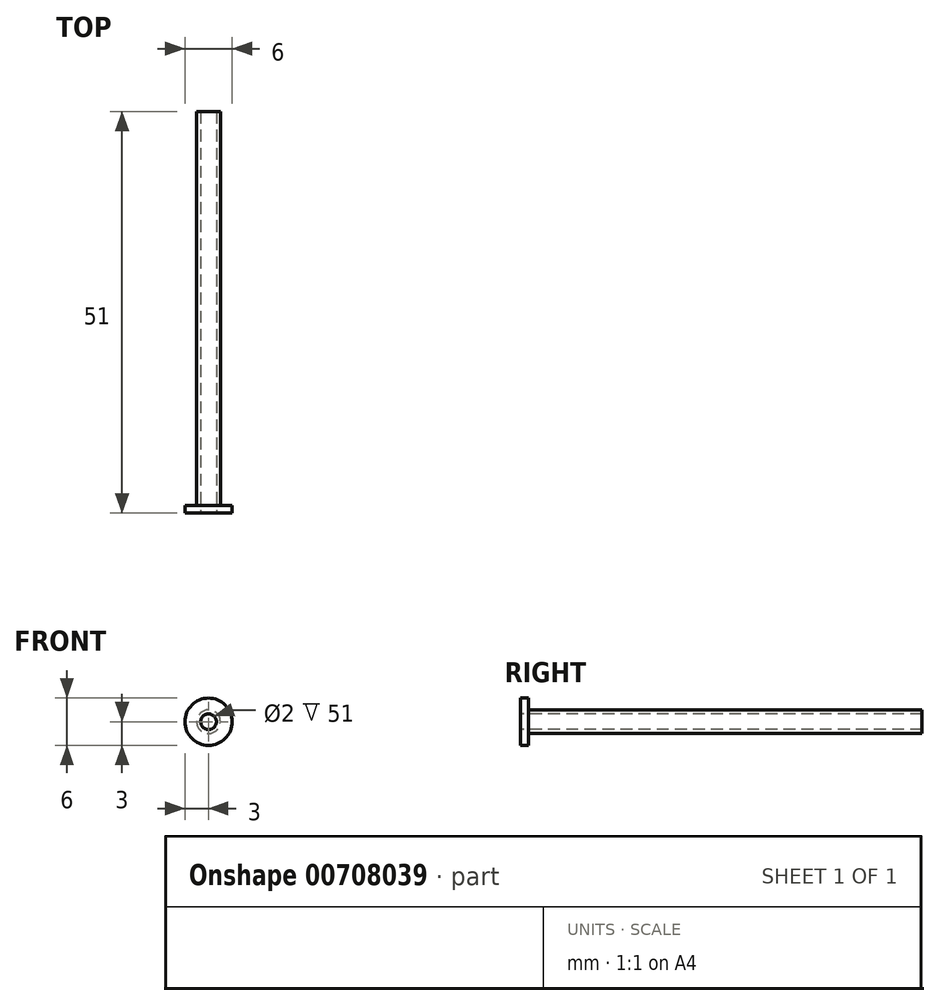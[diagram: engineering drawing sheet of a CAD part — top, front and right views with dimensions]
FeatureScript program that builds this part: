
annotation { "Feature Type Name" : "Feature", "Feature Type Description" : "" }
export const myFeature = defineFeature(function(context is Context, id is Id, definition is map)
    precondition{}
    {
        {
            var Q0;
            Q0=qCreatedBy(makeId("Front.planeOp"),FACE);
            var sketch = newSketch(context, id + "F0", { "sketchPlane" : qUnion([Q0])});
            skCircle(sketch, "E0", {"center": v(0, 0) * mm, "radius": 1.5 * mm});
            skSolve(sketch);
        }
        {
            var Q0;
            Q0 = qSketchRegion(id + "F0", true);
            extrude(context, id + "F1", {"entities" : qUnion([Q0]), "depth" : 50 * mm, "offsetDistance" : 25 * mm});
        }
        {
            var Q0;
            Q0=makeQuery(id+"F1.opExtrude","CAP_FACE",FACE,{"disambiguationData":[OSD([sQuery(id+"F0.wireOp",EDGE,"E0")])],"isStart":false});
            var sketch = newSketch(context, id + "F2", { "sketchPlane" : qUnion([Q0])});
            skCircle(sketch, "E1", {"center": v(0, 0) * mm, "radius": 1 * mm});
            skSolve(sketch);
        }
        {
            var Q0;
            Q0 = qSketchRegion(id + "F2", true);
            extrude(context, id + "F3", {"entities" : qUnion([Q0]), "operationType" : NewBodyOperationType.REMOVE, "endBound" : BoundingType.THROUGH_ALL, "oppositeDirection" : true, "depth" : 25 * mm, "offsetDistance" : 25 * mm});
        }
        {
            var Q0;
            Q0=makeQuery(id+"F1.opExtrude","CAP_FACE",FACE,{"disambiguationData":[OSD([sQuery(id+"F0.wireOp",EDGE,"E0")])],"isStart":false});
            var sketch = newSketch(context, id + "F4", { "sketchPlane" : qUnion([Q0])});
            skCircle(sketch, "E2", {"center": v(0, 0) * mm, "radius": 3 * mm});
            skSolve(sketch);
        }
        {
            var Q0;
            Q0=makeQuery(id+"F4.imprint","IMPRINT",FACE,{"disambiguationData":[TD([[makeQuery(id+"F4.imprint","IMPRINT",EDGE,{"derivedFrom":sQuery(id+"F4.wireOp",EDGE,"E2")}),1.0]])]});
            var sketch = newSketch(context, id + "F5", { "sketchPlane" : qUnion([Q0])});
            skCircle(sketch, "E3", {"center": v(0, 0) * mm, "radius": 1 * mm});
            skSolve(sketch);
        }
        {
            var Q0;
            Q0=makeQuery(id+"F4.imprint","IMPRINT",FACE,{"disambiguationData":[TD([[makeQuery(id+"F4.imprint","IMPRINT",EDGE,{"derivedFrom":makeQuery(id+"F1.opExtrude","CAP_EDGE",EDGE,{"disambiguationData":[OSD([sQuery(id+"F0.wireOp",EDGE,"E0")])],"isStart":false})}),1.0]])]});
            var Q1;
            Q1=makeQuery(id+"F5.imprint","IMPRINT",FACE,{"disambiguationData":[TD([[makeQuery(id+"F5.imprint","IMPRINT",EDGE,{"derivedFrom":makeQuery(id+"F4.imprint","IMPRINT",EDGE,{"derivedFrom":sQuery(id+"F4.wireOp",EDGE,"E2")})}),1.0]])]});
            extrude(context, id + "F6", {"entities" : qUnion([Q0, Q1]), "operationType" : NewBodyOperationType.ADD, "depth" : 1 * mm, "offsetDistance" : 25 * mm});
        }
    });
